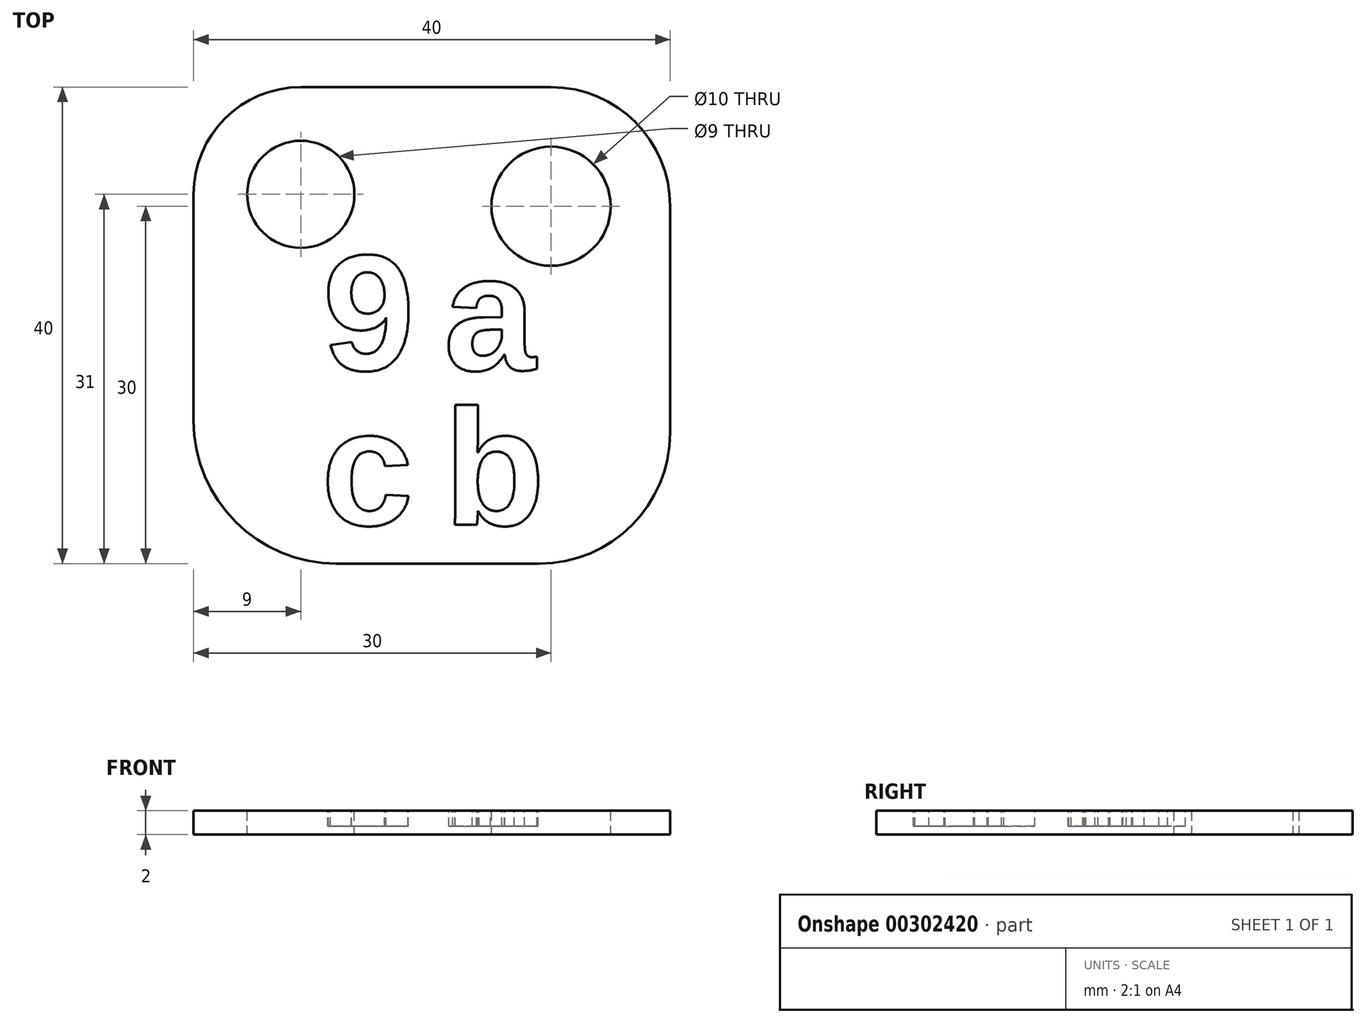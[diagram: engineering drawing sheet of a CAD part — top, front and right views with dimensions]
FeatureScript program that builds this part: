
annotation { "Feature Type Name" : "Feature", "Feature Type Description" : "" }
export const myFeature = defineFeature(function(context is Context, id is Id, definition is map)
    precondition{}
    {
        {
            var Q0;
            Q0=qCreatedBy(makeId("Top.planeOp"),FACE);
            var sketch = newSketch(context, id + "F0", { "sketchPlane" : qUnion([Q0])});
            skLineSegment(sketch, "E0.bottom", {"start": v(-11, 20) * mm, "end": v(10, 20) * mm});
            skLineSegment(sketch, "E0.top", {"start": v(-8, -20) * mm, "end": v(9, -20) * mm});
            skLineSegment(sketch, "E0.left", {"start": v(-20, 11) * mm, "end": v(-20, -8) * mm});
            skLineSegment(sketch, "E0.right", {"start": v(20, 10) * mm, "end": v(20, -9) * mm});
            skPoint(sketch, "E0.middle", {"position": v(0, 0) * mm});
            skPoint(sketch, "E1.visualSharp", {"position": v(-20, 20) * mm});
            skArc(sketch, "E1.filletArc", {"start": v(-11, 20) * mm, "mid": v(-17.36, 17.36) * mm, "end": v(-20, 11) * mm});
            skPoint(sketch, "E2.visualSharp", {"position": v(20, 20) * mm});
            skArc(sketch, "E2.filletArc", {"start": v(20, 10) * mm, "mid": v(17.07, 17.07) * mm, "end": v(10, 20) * mm});
            skPoint(sketch, "E3.visualSharp", {"position": v(20, -20) * mm});
            skArc(sketch, "E3.filletArc", {"start": v(9, -20) * mm, "mid": v(16.78, -16.78) * mm, "end": v(20, -9) * mm});
            skPoint(sketch, "E4.visualSharp", {"position": v(-20, -20) * mm});
            skArc(sketch, "E4.filletArc", {"start": v(-20, -8) * mm, "mid": v(-16.49, -16.49) * mm, "end": v(-8, -20) * mm});
            skSolve(sketch);
        }
        {
            var Q0;
            Q0=makeQuery(id+"F0.imprint","IMPRINT",FACE,{"disambiguationData":[TD([[makeQuery(id+"F0.imprint","IMPRINT",EDGE,{"derivedFrom":sQuery(id+"F0.wireOp",EDGE,"E0.bottom")}),-1.0]])]});
            extrude(context, id + "F1", {"entities" : qUnion([Q0]), "depth" : 2 * mm});
        }
        {
            var Q0;
            Q0=makeQuery(id+"F1.opExtrude","CAP_FACE",FACE,{"disambiguationData":[OSD([sQuery(id+"F0.wireOp",EDGE,"E0.bottom"),sQuery(id+"F0.wireOp",EDGE,"E0.top"),sQuery(id+"F0.wireOp",EDGE,"E0.left"),sQuery(id+"F0.wireOp",EDGE,"E0.right"),sQuery(id+"F0.wireOp",EDGE,"E1.filletArc"),sQuery(id+"F0.wireOp",EDGE,"E2.filletArc"),sQuery(id+"F0.wireOp",EDGE,"E3.filletArc"),sQuery(id+"F0.wireOp",EDGE,"E4.filletArc")])],"isStart":false});
            var sketch = newSketch(context, id + "F2", { "sketchPlane" : qUnion([Q0])});
            skLineSegment(sketch, "E5.bottom", {"start": v(-1, -6.75) * mm, "end": v(1, -6.75) * mm});
            skLineSegment(sketch, "E5.top", {"start": v(-1, -3.75) * mm, "end": v(1, -3.75) * mm});
            skLineSegment(sketch, "E5.left", {"start": v(-1, -6.75) * mm, "end": v(-1, -3.75) * mm});
            skLineSegment(sketch, "E5.right", {"start": v(1, -6.75) * mm, "end": v(1, -3.75) * mm});
            skPoint(sketch, "E5.middle", {"position": v(0, -5.25) * mm});
            skPoint(sketch, "E6", {"position": v(-1, -3.75) * mm});
            skText(sketch, "E7", { "text": "9", "fontName": "Arimo-Bold.ttf"});
            skText(sketch, "E8", { "text": "a", "fontName": "Arimo-Bold.ttf"});
            skText(sketch, "E9", { "text": "c", "fontName": "Arimo-Bold.ttf"});
            skText(sketch, "E10", { "text": "b", "fontName": "Arimo-Bold.ttf"});
            skCircle(sketch, "E11", {"center": v(-11, 11) * mm, "radius": 4.5 * mm});
            skCircle(sketch, "E12", {"center": v(10, 10) * mm, "radius": 5 * mm});
            const initialGuessF2  = {"E7": [-0.00917, -0.00375, 1, 0, 0.01], "E8": [0.001, -0.00375, 1, 0, 0.01], "E9": [-0.00928, -0.01675, 1, 0, 0.01], "E10": [0.001, -0.01675, 1, 0, 0.01]};
            skSetInitialGuess(sketch, initialGuessF2);
            skSolve(sketch);
        }
        {
            var Q0;
            Q0=makeQuery(id+"F2.imprint","IMPRINT",FACE,{"disambiguationData":[TD([[makeQuery(id+"F2.imprint","IMPRINT",EDGE,{"derivedFrom":sQuery(id+"F2.wireOp",EDGE,"E11")}),1.0]])]});
            var Q1;
            Q1=makeQuery(id+"F2.imprint","IMPRINT",FACE,{"disambiguationData":[TD([[makeQuery(id+"F2.imprint","IMPRINT",EDGE,{"derivedFrom":sQuery(id+"F2.wireOp",EDGE,"E12")}),1.0]])]});
            var Q2;
            Q2=makeQuery(id+"F2.imprint","IMPRINT",FACE,{"disambiguationData":[TD([[makeQuery(id+"F2.imprint","IMPRINT",EDGE,{"derivedFrom":sQuery(id+"F2.wireOp",EDGE,"OSNyVClo-oT1R-1Uys-fQUQ-b0kqkyuTcmnS")}),1.0]])]});
            var Q3;
            Q3=makeQuery(id+"F2.imprint","IMPRINT",FACE,{"disambiguationData":[TD([[makeQuery(id+"F2.imprint","IMPRINT",EDGE,{"derivedFrom":sQuery(id+"F2.wireOp",EDGE,"kPrrb8MY-uYxh-8OZQ-hykU-pqecz3mApg9A")}),1.0]])]});
            var Q4;
            Q4=sQuery(id+"F2.wireOp",EDGE,"E11");
            var Q5;
            Q5=sQuery(id+"F2.wireOp",EDGE,"E12");
            var Q6;
            Q6=sQuery(id+"F2.wireOp",EDGE,"OSNyVClo-oT1R-1Uys-fQUQ-b0kqkyuTcmnS");
            var Q7;
            Q7=sQuery(id+"F2.wireOp",EDGE,"kPrrb8MY-uYxh-8OZQ-hykU-pqecz3mApg9A");
            extrude(context, id + "F3", {"entities" : qUnion([Q0, Q1, Q2, Q3]), "operationType" : NewBodyOperationType.REMOVE, "surfaceEntities" : qUnion([Q4, Q5, Q6, Q7]), "oppositeDirection" : true, "depth" : 25 * mm});
        }
        {
            var Q0;
            Q0=makeQuery(id+"F2.imprint","IMPRINT",FACE,{"disambiguationData":[TD([[makeQuery(id+"F2.imprint","IMPRINT",EDGE,{"derivedFrom":sQuery(id+"F2.wireOp",EDGE,"E7.sketch_text.stroke-0")}),-1.0]])]});
            var Q1;
            Q1=makeQuery(id+"F2.imprint","IMPRINT",FACE,{"disambiguationData":[TD([[makeQuery(id+"F2.imprint","IMPRINT",EDGE,{"derivedFrom":sQuery(id+"F2.wireOp",EDGE,"E8.sketch_text.stroke-0")}),-1.0]])]});
            var Q2;
            Q2=makeQuery(id+"F2.imprint","IMPRINT",FACE,{"disambiguationData":[TD([[makeQuery(id+"F2.imprint","IMPRINT",EDGE,{"derivedFrom":sQuery(id+"F2.wireOp",EDGE,"E10.sketch_text.stroke-0")}),-1.0]])]});
            var Q3;
            Q3=makeQuery(id+"F2.imprint","IMPRINT",FACE,{"disambiguationData":[TD([[makeQuery(id+"F2.imprint","IMPRINT",EDGE,{"derivedFrom":sQuery(id+"F2.wireOp",EDGE,"E9.sketch_text.stroke-0")}),-1.0]])]});
            extrude(context, id + "F4", {"entities" : qUnion([Q0, Q1, Q2, Q3]), "operationType" : NewBodyOperationType.REMOVE, "oppositeDirection" : true, "depth" : 1.3 * mm});
        }
    });
